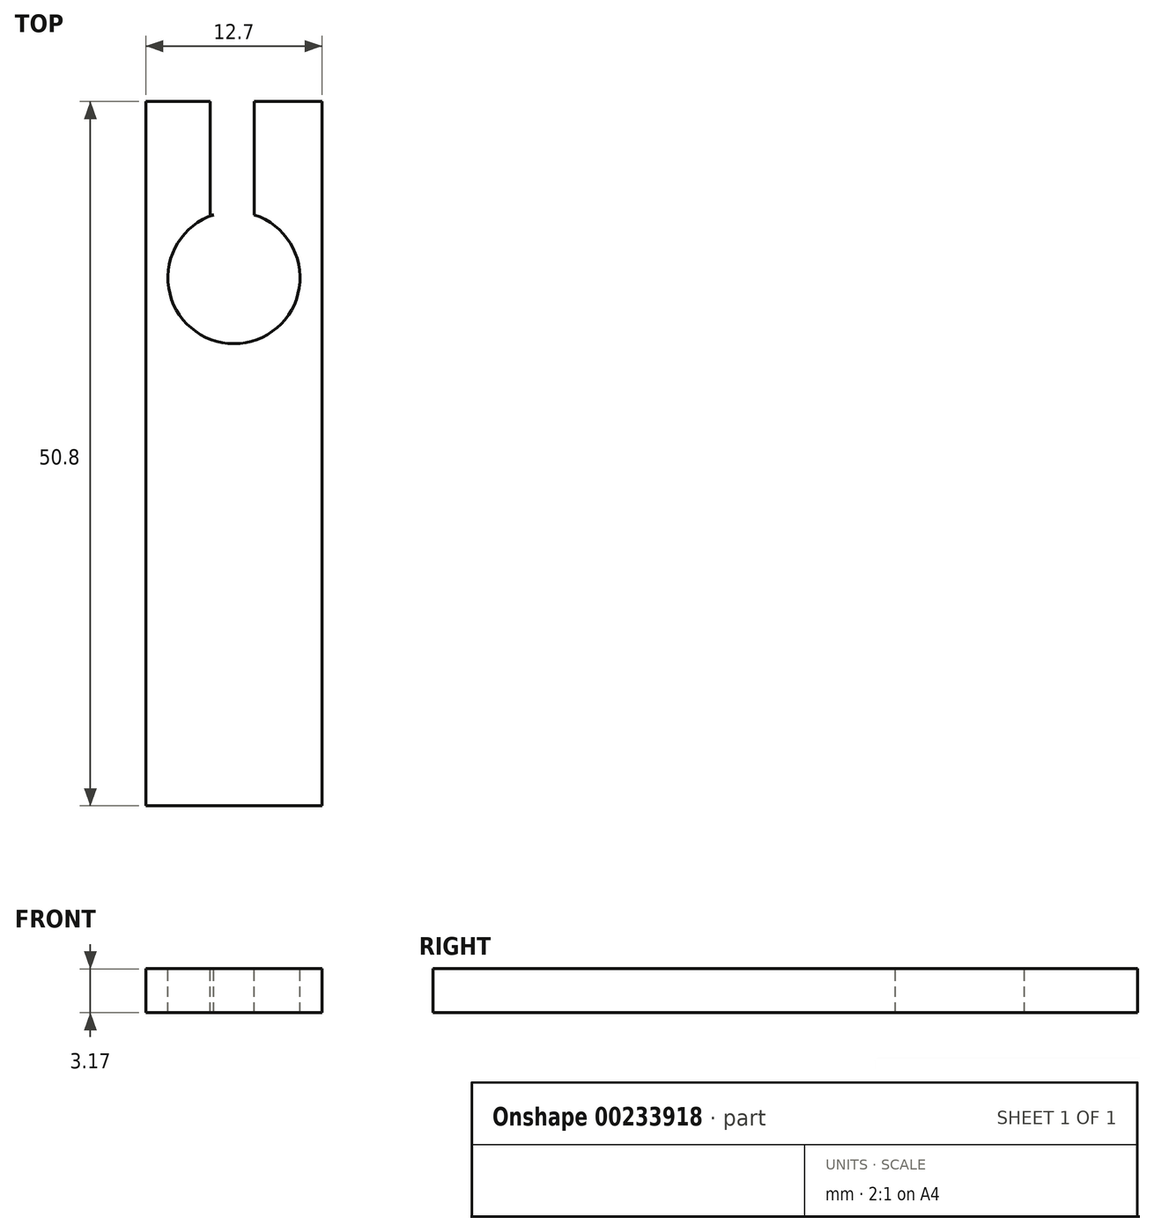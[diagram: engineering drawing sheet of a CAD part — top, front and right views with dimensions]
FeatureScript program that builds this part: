
annotation { "Feature Type Name" : "Feature", "Feature Type Description" : "" }
export const myFeature = defineFeature(function(context is Context, id is Id, definition is map)
    precondition{}
    {
        {
            var Q0;
            Q0=qCreatedBy(makeId("Top.planeOp"),FACE);
            var sketch = newSketch(context, id + "F0", { "sketchPlane" : qUnion([Q0])});
            skLineSegment(sketch, "E0.bottom", {"start": v(-6.35, 25.4) * mm, "end": v(6.35, 25.4) * mm});
            skLineSegment(sketch, "E0.top", {"start": v(-6.35, -25.4) * mm, "end": v(6.35, -25.4) * mm});
            skLineSegment(sketch, "E0.left", {"start": v(-6.35, 25.4) * mm, "end": v(-6.35, -25.4) * mm});
            skLineSegment(sketch, "E0.right", {"start": v(6.35, 25.4) * mm, "end": v(6.35, -25.4) * mm});
            skSolve(sketch);
        }
        {
            var Q0;
            Q0=makeQuery(id+"F0.imprint","IMPRINT",FACE,{"disambiguationData":[TD([[makeQuery(id+"F0.imprint","IMPRINT",EDGE,{"derivedFrom":sQuery(id+"F0.wireOp",EDGE,"E0.bottom")}),-1.0]])]});
            extrude(context, id + "F1", {"entities" : qUnion([Q0]), "depth" : 3.17 * mm});
        }
        {
            var Q0;
            Q0=makeQuery(id+"F1.opExtrude","CAP_FACE",FACE,{"disambiguationData":[OSD([sQuery(id+"F0.wireOp",EDGE,"E0.bottom"),sQuery(id+"F0.wireOp",EDGE,"E0.top"),sQuery(id+"F0.wireOp",EDGE,"E0.left"),sQuery(id+"F0.wireOp",EDGE,"E0.right")])],"isStart":false});
            var sketch = newSketch(context, id + "F2", { "sketchPlane" : qUnion([Q0])});
            skCircle(sketch, "E1", {"center": v(0, 12.7) * mm, "radius": 4.76 * mm});
            skSolve(sketch);
        }
        {
            var Q0;
            Q0=makeQuery(id+"F2.imprint","IMPRINT",FACE,{"disambiguationData":[TD([[makeQuery(id+"F2.imprint","IMPRINT",EDGE,{"derivedFrom":sQuery(id+"F2.wireOp",EDGE,"E1")}),1.0]])]});
            var Q1;
            Q1=makeQuery(id+"F1.opExtrude","CAP_FACE",FACE,{"disambiguationData":[OSD([sQuery(id+"F0.wireOp",EDGE,"E0.bottom"),sQuery(id+"F0.wireOp",EDGE,"E0.top"),sQuery(id+"F0.wireOp",EDGE,"E0.left"),sQuery(id+"F0.wireOp",EDGE,"E0.right")])],"isStart":true});
            extrude(context, id + "F3", {"entities" : qUnion([Q0]), "operationType" : NewBodyOperationType.REMOVE, "endBound" : BoundingType.UP_TO_SURFACE, "oppositeDirection" : true, "endBoundEntityFace" : qUnion([Q1]), "depth" : 25.4 * mm});
        }
        {
            var Q0;
            Q0=makeQuery(id+"F1.opExtrude","CAP_FACE",FACE,{"disambiguationData":[OSD([sQuery(id+"F0.wireOp",EDGE,"E0.bottom"),sQuery(id+"F0.wireOp",EDGE,"E0.top"),sQuery(id+"F0.wireOp",EDGE,"E0.left"),sQuery(id+"F0.wireOp",EDGE,"E0.right")])],"isStart":false});
            var sketch = newSketch(context, id + "F4", { "sketchPlane" : qUnion([Q0])});
            skLineSegment(sketch, "E2.bottom", {"start": v(-1.71, 25.4) * mm, "end": v(1.46, 25.4) * mm});
            skLineSegment(sketch, "E2.top", {"start": v(-1.71, 17.23) * mm, "end": v(1.46, 17.23) * mm});
            skLineSegment(sketch, "E2.left", {"start": v(-1.71, 25.4) * mm, "end": v(-1.71, 17.23) * mm});
            skLineSegment(sketch, "E2.right", {"start": v(1.46, 25.4) * mm, "end": v(1.46, 17.23) * mm});
            skSolve(sketch);
        }
        {
            var Q0;
            Q0=makeQuery(id+"F4.imprint","IMPRINT",FACE,{"disambiguationData":[TD([[makeQuery(id+"F4.imprint","IMPRINT",EDGE,{"derivedFrom":sQuery(id+"F4.wireOp",EDGE,"E2.bottom")}),-1.0]])]});
            var Q1;
            Q1=makeQuery(id+"F1.opExtrude","CAP_FACE",FACE,{"disambiguationData":[OSD([sQuery(id+"F0.wireOp",EDGE,"E0.bottom"),sQuery(id+"F0.wireOp",EDGE,"E0.top"),sQuery(id+"F0.wireOp",EDGE,"E0.left"),sQuery(id+"F0.wireOp",EDGE,"E0.right")])],"isStart":true});
            extrude(context, id + "F5", {"entities" : qUnion([Q0]), "operationType" : NewBodyOperationType.REMOVE, "endBound" : BoundingType.UP_TO_SURFACE, "oppositeDirection" : true, "endBoundEntityFace" : qUnion([Q1]), "depth" : 25.4 * mm});
        }
    });
